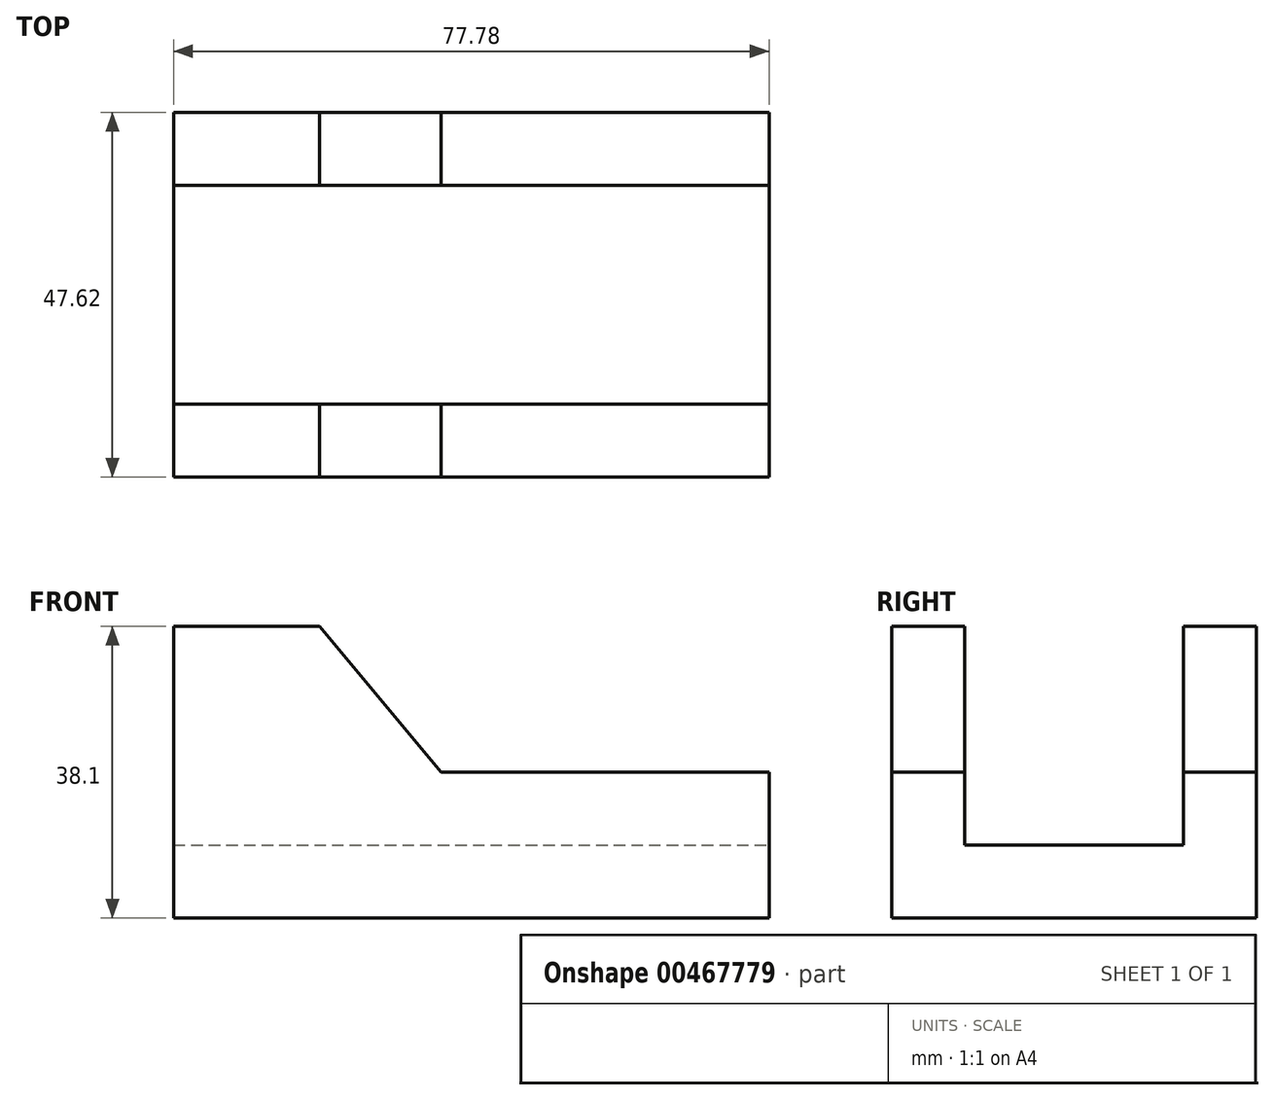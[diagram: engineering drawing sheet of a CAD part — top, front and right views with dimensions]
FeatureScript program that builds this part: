
annotation { "Feature Type Name" : "Feature", "Feature Type Description" : "" }
export const myFeature = defineFeature(function(context is Context, id is Id, definition is map)
    precondition{}
    {
        {
            var Q0;
            Q0=qCreatedBy(makeId("Top.planeOp"),FACE);
            var sketch = newSketch(context, id + "F0", { "sketchPlane" : qUnion([Q0])});
            skLineSegment(sketch, "E0.bottom", {"start": v(-38.9, 23.81) * mm, "end": v(38.9, 23.81) * mm});
            skLineSegment(sketch, "E0.top", {"start": v(-38.9, -23.81) * mm, "end": v(38.9, -23.81) * mm});
            skLineSegment(sketch, "E0.left", {"start": v(-38.9, 23.81) * mm, "end": v(-38.9, -23.81) * mm});
            skLineSegment(sketch, "E0.right", {"start": v(38.9, 23.81) * mm, "end": v(38.9, -23.81) * mm});
            skPoint(sketch, "E0.middle", {"position": v(0, 0) * mm});
            skSolve(sketch);
        }
        {
            var Q0;
            Q0 = qSketchRegion(id + "F0", true);
            extrude(context, id + "F1", {"entities" : qUnion([Q0]), "depth" : 9.52 * mm});
        }
        {
            var Q0;
            Q0=makeQuery(id+"F1.opExtrude","SWEPT_FACE",FACE,{"disambiguationData":[OSD([sQuery(id+"F0.wireOp",EDGE,"E0.top")])]});
            var sketch = newSketch(context, id + "F2", { "sketchPlane" : qUnion([Q0])});
            skLineSegment(sketch, "E1", {"start": v(-38.9, 9.53) * mm, "end": v(-38.9, 38.1) * mm});
            skLineSegment(sketch, "E2", {"start": v(-38.9, 38.1) * mm, "end": v(-19.84, 38.1) * mm});
            skLineSegment(sketch, "E3", {"start": v(-19.84, 38.1) * mm, "end": v(-3.97, 19.05) * mm});
            skLineSegment(sketch, "E4", {"start": v(-3.97, 19.05) * mm, "end": v(38.9, 19.05) * mm});
            skLineSegment(sketch, "E5", {"start": v(38.9, 19.05) * mm, "end": v(38.9, 9.53) * mm});
            skLineSegment(sketch, "E6", {"start": v(38.9, 9.53) * mm, "end": v(-38.9, 9.53) * mm});
            skSolve(sketch);
        }
        {
            var Q0;
            Q0=makeQuery(id+"F2.imprint","IMPRINT",FACE,{"disambiguationData":[TD([[makeQuery(id+"F2.imprint","IMPRINT",EDGE,{"derivedFrom":sQuery(id+"F2.wireOp",EDGE,"E1")}),-1.0]])]});
            extrude(context, id + "F3", {"entities" : qUnion([Q0]), "operationType" : NewBodyOperationType.ADD, "oppositeDirection" : true, "depth" : 9.52 * mm});
        }
        {
            var Q0;
            Q0=makeQuery(id+"F1.opExtrude","SWEPT_BODY",BODY,{"disambiguationData":[OSD([sQuery(id+"F0.wireOp",EDGE,"E0.bottom"),sQuery(id+"F0.wireOp",EDGE,"E0.top"),sQuery(id+"F0.wireOp",EDGE,"E0.left"),sQuery(id+"F0.wireOp",EDGE,"E0.right")])]});
            var Q1;
            Q1=qCreatedBy(makeId("Front.planeOp"),FACE);
            mirror(context, id + "F4", {"operationType" : NewBodyOperationType.ADD, "entities" : qUnion([Q0]), "mirrorPlane" : qUnion([Q1])});
        }
    });
